# Revit family: Resideo_WallMountKit_Evotouch_ATF600a
name_source: partatom
category: Generic Models
units: mm (PartAtom-declared; Revit-internal decimal feet)

## family parameters
Can host rebar = No
Cut with Voids When Loaded = No
Host = Face
OmniClass Number = 23.75.65.11.11
OmniClass Title = Heating Controllers
Part Type = Normal
Room Calculation Point = No
Round Connector Dimension = Use Diameter
Shared = No

## types (1)
- ATF600
    Assembly Code = E1090900
    AssetType = Fixed
    BIMObjectName = Resideo_WallMountKit_Evotouch_ATF600
    ClassificationName = Uniclass2015
    ClassificationValue = Pr_20_85_09_54
    Cost = 0 $
    Default Elevation = 0 mm  [stored 0 ft]
    Description = EVOHOME WI-FI  WALL MOUNTED PACK
    DocumentationCertificates = https://www.bimstore.co
    DocumentationInstallationGuide = https://www.bimstore.co
    DocumentationLiterature = https://www.bimstore.co
    DocumentationMaintenance = https://www.bimstore.co
    DocumentationTechnical = https://www.bimstore.co
    DurationUnit = Year
    ExpectedLife = 0
    IfcExportAs = IfcBuildingElementProxyType
    IfcExportType = IfcBuildingElementProxyType.USERDEFINED
    Keynote = W
    Manufacturer = Resideo
    ManufacturerName = Resideo
    Model = ATF600
    ModelNumber = ATF600
    ModelReference = EVOHOME WI-FI  WALL MOUNTED PACK
    NBSDescription = Mounting brackets
    NBSObjectName = Resideo - Mounting brackets
    NominalDepth = 17 mm
    NominalHeight = 86 mm  [stored 0.282152 ft]
    NominalLength = 105 mm  [stored 0.344488 ft]
    PrimaryMaterial = Resideo - Plastic - White
    ProductionYear = 2022
    Size = 16.7mm (D) x 86mm (H) x 105mm (L)
    Type Comments = EVOHOME WI-FI  WALL MOUNTED PACK
    TypeName = ATF600 - EVOHOME WI-FI  WALL MOUNTED PACK
    URL = https://www.resideo.com
    WarrantyDurationLabor = 0
    WarrantyDurationParts = 0
    WarrantyDurationUnit = Year
    WarrantyGuarantorLabor = https://www.resideo.com
    WarrantyGuarantorParts = https://www.resideo.com
    _BSBibleVersion = 16
    _BimSpecGuid = 0
    _CurrentRevision = 1
    _DistributedBy = https://www.bimstore.co
    _ObjectUserGuide = https://www.bimstore.co

note: [stored X ft] marks values corroborated as IEEE doubles in the binary element streams (Revit-internal decimal feet)

## geometry (parser evidence)
native form markers: Sweep x2
no freeform markers — native parametric forms only
